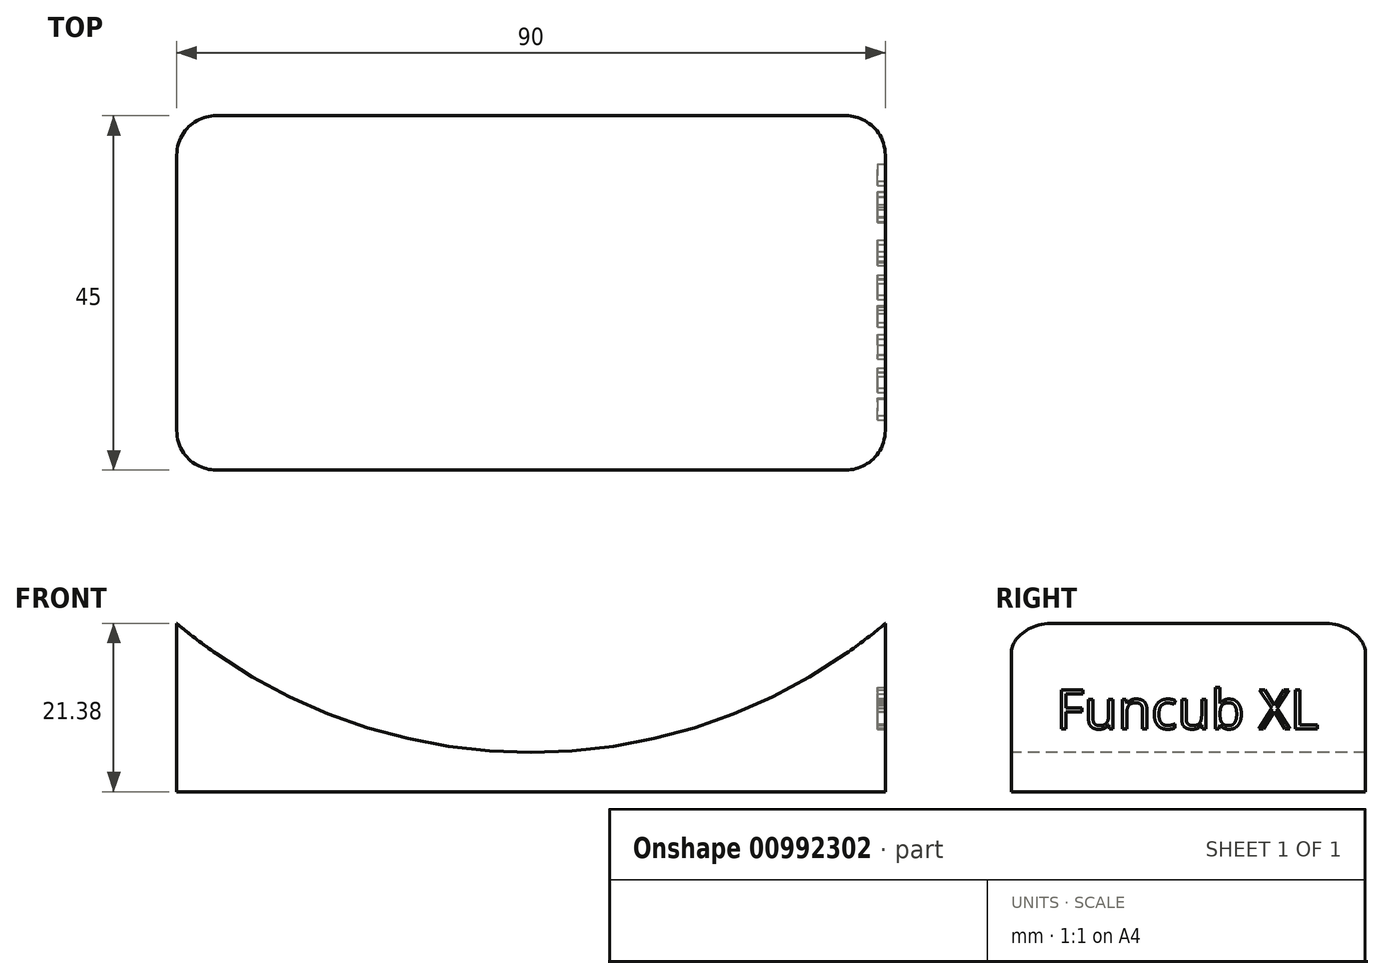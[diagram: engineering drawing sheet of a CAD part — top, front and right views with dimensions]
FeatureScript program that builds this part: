
annotation { "Feature Type Name" : "Feature", "Feature Type Description" : "" }
export const myFeature = defineFeature(function(context is Context, id is Id, definition is map)
    precondition{}
    {
        {
            var Q0;
            Q0=qCreatedBy(makeId("Top.planeOp"),FACE);
            var sketch = newSketch(context, id + "F0", { "sketchPlane" : qUnion([Q0])});
            skLineSegment(sketch, "E0.bottom", {"start": v(-40, 22.5) * mm, "end": v(40, 22.5) * mm});
            skLineSegment(sketch, "E0.top", {"start": v(-40, -22.5) * mm, "end": v(40, -22.5) * mm});
            skLineSegment(sketch, "E0.left", {"start": v(-45, 17.5) * mm, "end": v(-45, -17.5) * mm});
            skLineSegment(sketch, "E0.right", {"start": v(45, 17.5) * mm, "end": v(45, -17.5) * mm});
            skPoint(sketch, "E1.visualSharp", {"position": v(-45, 22.5) * mm});
            skArc(sketch, "E1.filletArc", {"start": v(-40, 22.5) * mm, "mid": v(-43.54, 21.04) * mm, "end": v(-45, 17.5) * mm});
            skPoint(sketch, "E2.visualSharp", {"position": v(-45, -22.5) * mm});
            skArc(sketch, "E2.filletArc", {"start": v(-45, -17.5) * mm, "mid": v(-43.54, -21.04) * mm, "end": v(-40, -22.5) * mm});
            skPoint(sketch, "E3.visualSharp", {"position": v(45, -22.5) * mm});
            skArc(sketch, "E3.filletArc", {"start": v(40, -22.5) * mm, "mid": v(43.54, -21.04) * mm, "end": v(45, -17.5) * mm});
            skPoint(sketch, "E4.visualSharp", {"position": v(45, 22.5) * mm});
            skArc(sketch, "E4.filletArc", {"start": v(45, 17.5) * mm, "mid": v(43.54, 21.04) * mm, "end": v(40, 22.5) * mm});
            skSolve(sketch);
        }
        {
            var Q0;
            Q0 = qSketchRegion(id + "F0", true);
            extrude(context, id + "F1", {"entities" : qUnion([Q0]), "depth" : 40 * mm, "offsetDistance" : 25 * mm});
        }
        {
            var Q0;
            Q0=makeQuery(id+"F1.opExtrude","SWEPT_FACE",FACE,{"disambiguationData":[OSD([sQuery(id+"F0.wireOp",EDGE,"E0.top")])]});
            var sketch = newSketch(context, id + "F2", { "sketchPlane" : qUnion([Q0])});
            skArc(sketch, "E5", {"start": v(-60.62, 40) * mm, "mid": v(0, 5) * mm, "end": v(60.62, 40) * mm});
            skLineSegment(sketch, "E6", {"start": v(-60.62, 40) * mm, "end": v(60.62, 40) * mm});
            skSolve(sketch);
        }
        {
            var Q0;
            Q0 = qSketchRegion(id + "F2", true);
            extrude(context, id + "F3", {"entities" : qUnion([Q0]), "operationType" : NewBodyOperationType.REMOVE, "endBound" : BoundingType.THROUGH_ALL, "oppositeDirection" : true, "depth" : 25 * mm, "offsetDistance" : 25 * mm});
        }
        {
            var Q0;
            Q0=makeQuery(id+"F1.opExtrude","SWEPT_FACE",FACE,{"disambiguationData":[OSD([sQuery(id+"F0.wireOp",EDGE,"E0.right")])]});
            var sketch = newSketch(context, id + "F4", { "sketchPlane" : qUnion([Q0])});
            skText(sketch, "E7", { "text": "Funcub XL", "fontName": "OpenSans-Regular.ttf"});
            const initialGuessF4  = {"E7": [-0.01682, 0.008, 1, 0, 0.005]};
            skSetInitialGuess(sketch, initialGuessF4);
            skSolve(sketch);
        }
        {
            var Q0;
            Q0 = qSketchRegion(id + "F4", true);
            extrude(context, id + "F5", {"entities" : qUnion([Q0]), "operationType" : NewBodyOperationType.REMOVE, "oppositeDirection" : true, "depth" : 1 * mm, "offsetDistance" : 25 * mm});
        }
    });
